annotation { "Feature Type Name" : "Feature", "Feature Type Description" : "" }
export const myFeature = defineFeature(function(context is Context, id is Id, definition is map)
    precondition{}
    {
        {
            var Q0;
            Q0=qCreatedBy(makeId("Front.planeOp"),FACE);
            var sketch = newSketch(context, id + "F0", { "sketchPlane" : qUnion([Q0])});
            skLineSegment(sketch, "E0", {"start": v(0, 0) * mm, "end": v(0, 115.04) * mm, "construction": true});
            skLineSegment(sketch, "E1", {"start": v(0, 54.34) * mm, "end": v(32, 54.34) * mm});
            skLineSegment(sketch, "E2", {"start": v(0, 0) * mm, "end": v(15.73, 0) * mm});
            skFitSpline(sketch, "E3", {"points": [v(32, 54.34) * mm, v(50.29, 47.3) * mm, v(51.95, 34.67) * mm, v(46.18, 14.3) * mm, v(15.73, 0) * mm], "startDerivative": vector(95.6, 0) * mm, "endDerivative": vector(-87.5, 0) * mm});
            skLineSegment(sketch, "E4", {"start": v(0, 54.34) * mm, "end": v(0, 0) * mm});
            skSolve(sketch);
        }
        {
            var Q0;
            Q0=qSketchRegion(id+"F0",true);
            var Q1;
            Q1=sQuery(id+"F0.wireOp",EDGE,"E0");
            revolve(context, id + "F1", {"entities" : qUnion([Q0]), "axis" : qUnion([Q1]), "revolveType" : RevolveType.FULL});
        }
        {
            var Q0;
            Q0=qCreatedBy(makeId("Front.planeOp"),FACE);
            cPlane(context, id + "F2", {"entities" : qUnion([Q0]), "cplaneType" : CPlaneType.OFFSET, "offset" : 55 * mm, "width" : 150 * mm, "height" : 150 * mm});
        }
        {
            var Q0;
            Q0=qCreatedBy(id+"F2.planeOp",FACE);
            var sketch = newSketch(context, id + "F3", { "sketchPlane" : qUnion([Q0])});
            skText(sketch, "E5", { "text": "JAY WILLIAMS", "fontName": "OpenSans-Bold.ttf"});
            const initialGuessF3  = {"E5": [-0.04412, 0.03506, 1, 0, 0.00915]};
            skSetInitialGuess(sketch, initialGuessF3);
            skSolve(sketch);
        }
        {
            var Q0;
            Q0=qSketchRegion(id+"F3",true);
            var Q1;
            Q1=qCreatedBy(makeId("Front.planeOp"),FACE);
            extrude(context, id + "F4", {"entities" : qUnion([Q0]), "endBound" : BoundingType.UP_TO_SURFACE, "oppositeDirection" : true, "endBoundEntityFace" : qUnion([Q1]), "depth" : 25 * mm});
        }
        {
            var Q0;
            Q0=makeQuery(id+"F1.opRevolve","SWEPT_BODY",BODY,{"disambiguationData":[OSD([sQuery(id+"F0.wireOp",EDGE,"E1"),sQuery(id+"F0.wireOp",EDGE,"E2"),sQuery(id+"F0.wireOp",EDGE,"E3"),sQuery(id+"F0.wireOp",EDGE,"E4")])]});
            var Q1;
            Q1=makeQuery(id+"F4.opExtrude","SWEPT_BODY",BODY,{"disambiguationData":[OSD([sQuery(id+"F3.wireOp",EDGE,"E5.sketch_text.stroke-0"),sQuery(id+"F3.wireOp",EDGE,"E5.sketch_text.stroke-1"),sQuery(id+"F3.wireOp",EDGE,"E5.sketch_text.stroke-2"),sQuery(id+"F3.wireOp",EDGE,"E5.sketch_text.stroke-3"),sQuery(id+"F3.wireOp",EDGE,"E5.sketch_text.stroke-4"),sQuery(id+"F3.wireOp",EDGE,"E5.sketch_text.stroke-5"),sQuery(id+"F3.wireOp",EDGE,"E5.sketch_text.stroke-6"),sQuery(id+"F3.wireOp",EDGE,"E5.sketch_text.stroke-7"),sQuery(id+"F3.wireOp",EDGE,"E5.sketch_text.stroke-8"),sQuery(id+"F3.wireOp",EDGE,"E5.sketch_text.stroke-9")])]});
            var Q2;
            Q2=makeQuery(id+"F4.opExtrude","SWEPT_BODY",BODY,{"disambiguationData":[OSD([sQuery(id+"F3.wireOp",EDGE,"E5.sketch_text.stroke-10"),sQuery(id+"F3.wireOp",EDGE,"E5.sketch_text.stroke-11"),sQuery(id+"F3.wireOp",EDGE,"E5.sketch_text.stroke-12"),sQuery(id+"F3.wireOp",EDGE,"E5.sketch_text.stroke-13"),sQuery(id+"F3.wireOp",EDGE,"E5.sketch_text.stroke-14"),sQuery(id+"F3.wireOp",EDGE,"E5.sketch_text.stroke-15"),sQuery(id+"F3.wireOp",EDGE,"E5.sketch_text.stroke-16"),sQuery(id+"F3.wireOp",EDGE,"E5.sketch_text.stroke-17"),sQuery(id+"F3.wireOp",EDGE,"E5.sketch_text.stroke-18"),sQuery(id+"F3.wireOp",EDGE,"E5.sketch_text.stroke-19"),sQuery(id+"F3.wireOp",EDGE,"E5.sketch_text.stroke-20"),sQuery(id+"F3.wireOp",EDGE,"E5.sketch_text.stroke-21")])]});
            var Q3;
            Q3=makeQuery(id+"F4.opExtrude","SWEPT_BODY",BODY,{"disambiguationData":[OSD([sQuery(id+"F3.wireOp",EDGE,"E5.sketch_text.stroke-22"),sQuery(id+"F3.wireOp",EDGE,"E5.sketch_text.stroke-23"),sQuery(id+"F3.wireOp",EDGE,"E5.sketch_text.stroke-24"),sQuery(id+"F3.wireOp",EDGE,"E5.sketch_text.stroke-25"),sQuery(id+"F3.wireOp",EDGE,"E5.sketch_text.stroke-26"),sQuery(id+"F3.wireOp",EDGE,"E5.sketch_text.stroke-27"),sQuery(id+"F3.wireOp",EDGE,"E5.sketch_text.stroke-28"),sQuery(id+"F3.wireOp",EDGE,"E5.sketch_text.stroke-29"),sQuery(id+"F3.wireOp",EDGE,"E5.sketch_text.stroke-30")])]});
            var Q4;
            Q4=makeQuery(id+"F4.opExtrude","SWEPT_BODY",BODY,{"disambiguationData":[OSD([sQuery(id+"F3.wireOp",EDGE,"E5.sketch_text.stroke-31"),sQuery(id+"F3.wireOp",EDGE,"E5.sketch_text.stroke-32"),sQuery(id+"F3.wireOp",EDGE,"E5.sketch_text.stroke-33"),sQuery(id+"F3.wireOp",EDGE,"E5.sketch_text.stroke-34"),sQuery(id+"F3.wireOp",EDGE,"E5.sketch_text.stroke-35"),sQuery(id+"F3.wireOp",EDGE,"E5.sketch_text.stroke-36"),sQuery(id+"F3.wireOp",EDGE,"E5.sketch_text.stroke-37"),sQuery(id+"F3.wireOp",EDGE,"E5.sketch_text.stroke-38"),sQuery(id+"F3.wireOp",EDGE,"E5.sketch_text.stroke-39"),sQuery(id+"F3.wireOp",EDGE,"E5.sketch_text.stroke-40"),sQuery(id+"F3.wireOp",EDGE,"E5.sketch_text.stroke-41"),sQuery(id+"F3.wireOp",EDGE,"E5.sketch_text.stroke-42"),sQuery(id+"F3.wireOp",EDGE,"E5.sketch_text.stroke-43"),sQuery(id+"F3.wireOp",EDGE,"E5.sketch_text.stroke-44"),sQuery(id+"F3.wireOp",EDGE,"E5.sketch_text.stroke-45"),sQuery(id+"F3.wireOp",EDGE,"E5.sketch_text.stroke-46"),sQuery(id+"F3.wireOp",EDGE,"E5.sketch_text.stroke-47"),sQuery(id+"F3.wireOp",EDGE,"E5.sketch_text.stroke-48"),sQuery(id+"F3.wireOp",EDGE,"E5.sketch_text.stroke-49"),sQuery(id+"F3.wireOp",EDGE,"E5.sketch_text.stroke-50"),sQuery(id+"F3.wireOp",EDGE,"E5.sketch_text.stroke-51"),sQuery(id+"F3.wireOp",EDGE,"E5.sketch_text.stroke-52"),sQuery(id+"F3.wireOp",EDGE,"E5.sketch_text.stroke-53"),sQuery(id+"F3.wireOp",EDGE,"E5.sketch_text.stroke-54")])]});
            var Q5;
            Q5=makeQuery(id+"F4.opExtrude","SWEPT_BODY",BODY,{"disambiguationData":[OSD([sQuery(id+"F3.wireOp",EDGE,"E5.sketch_text.stroke-55"),sQuery(id+"F3.wireOp",EDGE,"E5.sketch_text.stroke-56"),sQuery(id+"F3.wireOp",EDGE,"E5.sketch_text.stroke-57"),sQuery(id+"F3.wireOp",EDGE,"E5.sketch_text.stroke-58")])]});
            var Q6;
            Q6=makeQuery(id+"F4.opExtrude","SWEPT_BODY",BODY,{"disambiguationData":[OSD([sQuery(id+"F3.wireOp",EDGE,"E5.sketch_text.stroke-59"),sQuery(id+"F3.wireOp",EDGE,"E5.sketch_text.stroke-60"),sQuery(id+"F3.wireOp",EDGE,"E5.sketch_text.stroke-61"),sQuery(id+"F3.wireOp",EDGE,"E5.sketch_text.stroke-62"),sQuery(id+"F3.wireOp",EDGE,"E5.sketch_text.stroke-63"),sQuery(id+"F3.wireOp",EDGE,"E5.sketch_text.stroke-64")])]});
            var Q7;
            Q7=makeQuery(id+"F4.opExtrude","SWEPT_BODY",BODY,{"disambiguationData":[OSD([sQuery(id+"F3.wireOp",EDGE,"E5.sketch_text.stroke-65"),sQuery(id+"F3.wireOp",EDGE,"E5.sketch_text.stroke-66"),sQuery(id+"F3.wireOp",EDGE,"E5.sketch_text.stroke-67"),sQuery(id+"F3.wireOp",EDGE,"E5.sketch_text.stroke-68"),sQuery(id+"F3.wireOp",EDGE,"E5.sketch_text.stroke-69"),sQuery(id+"F3.wireOp",EDGE,"E5.sketch_text.stroke-70")])]});
            var Q8;
            Q8=makeQuery(id+"F4.opExtrude","SWEPT_BODY",BODY,{"disambiguationData":[OSD([sQuery(id+"F3.wireOp",EDGE,"E5.sketch_text.stroke-71"),sQuery(id+"F3.wireOp",EDGE,"E5.sketch_text.stroke-72"),sQuery(id+"F3.wireOp",EDGE,"E5.sketch_text.stroke-73"),sQuery(id+"F3.wireOp",EDGE,"E5.sketch_text.stroke-74")])]});
            var Q9;
            Q9=makeQuery(id+"F4.opExtrude","SWEPT_BODY",BODY,{"disambiguationData":[OSD([sQuery(id+"F3.wireOp",EDGE,"E5.sketch_text.stroke-75"),sQuery(id+"F3.wireOp",EDGE,"E5.sketch_text.stroke-76"),sQuery(id+"F3.wireOp",EDGE,"E5.sketch_text.stroke-77"),sQuery(id+"F3.wireOp",EDGE,"E5.sketch_text.stroke-78"),sQuery(id+"F3.wireOp",EDGE,"E5.sketch_text.stroke-79"),sQuery(id+"F3.wireOp",EDGE,"E5.sketch_text.stroke-80"),sQuery(id+"F3.wireOp",EDGE,"E5.sketch_text.stroke-81"),sQuery(id+"F3.wireOp",EDGE,"E5.sketch_text.stroke-82"),sQuery(id+"F3.wireOp",EDGE,"E5.sketch_text.stroke-83"),sQuery(id+"F3.wireOp",EDGE,"E5.sketch_text.stroke-84"),sQuery(id+"F3.wireOp",EDGE,"E5.sketch_text.stroke-85"),sQuery(id+"F3.wireOp",EDGE,"E5.sketch_text.stroke-86")])]});
            var Q10;
            Q10=makeQuery(id+"F4.opExtrude","SWEPT_BODY",BODY,{"disambiguationData":[OSD([sQuery(id+"F3.wireOp",EDGE,"E5.sketch_text.stroke-87"),sQuery(id+"F3.wireOp",EDGE,"E5.sketch_text.stroke-88"),sQuery(id+"F3.wireOp",EDGE,"E5.sketch_text.stroke-89"),sQuery(id+"F3.wireOp",EDGE,"E5.sketch_text.stroke-90"),sQuery(id+"F3.wireOp",EDGE,"E5.sketch_text.stroke-91"),sQuery(id+"F3.wireOp",EDGE,"E5.sketch_text.stroke-92"),sQuery(id+"F3.wireOp",EDGE,"E5.sketch_text.stroke-93"),sQuery(id+"F3.wireOp",EDGE,"E5.sketch_text.stroke-94"),sQuery(id+"F3.wireOp",EDGE,"E5.sketch_text.stroke-95"),sQuery(id+"F3.wireOp",EDGE,"E5.sketch_text.stroke-96"),sQuery(id+"F3.wireOp",EDGE,"E5.sketch_text.stroke-97"),sQuery(id+"F3.wireOp",EDGE,"E5.sketch_text.stroke-98"),sQuery(id+"F3.wireOp",EDGE,"E5.sketch_text.stroke-99"),sQuery(id+"F3.wireOp",EDGE,"E5.sketch_text.stroke-100"),sQuery(id+"F3.wireOp",EDGE,"E5.sketch_text.stroke-101"),sQuery(id+"F3.wireOp",EDGE,"E5.sketch_text.stroke-102"),sQuery(id+"F3.wireOp",EDGE,"E5.sketch_text.stroke-103"),sQuery(id+"F3.wireOp",EDGE,"E5.sketch_text.stroke-104"),sQuery(id+"F3.wireOp",EDGE,"E5.sketch_text.stroke-105")])]});
            var Q11;
            Q11=makeQuery(id+"F4.opExtrude","SWEPT_BODY",BODY,{"disambiguationData":[OSD([sQuery(id+"F3.wireOp",EDGE,"E5.sketch_text.stroke-106"),sQuery(id+"F3.wireOp",EDGE,"E5.sketch_text.stroke-107"),sQuery(id+"F3.wireOp",EDGE,"E5.sketch_text.stroke-108"),sQuery(id+"F3.wireOp",EDGE,"E5.sketch_text.stroke-109"),sQuery(id+"F3.wireOp",EDGE,"E5.sketch_text.stroke-110"),sQuery(id+"F3.wireOp",EDGE,"E5.sketch_text.stroke-111"),sQuery(id+"F3.wireOp",EDGE,"E5.sketch_text.stroke-112"),sQuery(id+"F3.wireOp",EDGE,"E5.sketch_text.stroke-113"),sQuery(id+"F3.wireOp",EDGE,"E5.sketch_text.stroke-114"),sQuery(id+"F3.wireOp",EDGE,"E5.sketch_text.stroke-115"),sQuery(id+"F3.wireOp",EDGE,"E5.sketch_text.stroke-116"),sQuery(id+"F3.wireOp",EDGE,"E5.sketch_text.stroke-117"),sQuery(id+"F3.wireOp",EDGE,"E5.sketch_text.stroke-118"),sQuery(id+"F3.wireOp",EDGE,"E5.sketch_text.stroke-119"),sQuery(id+"F3.wireOp",EDGE,"E5.sketch_text.stroke-120"),sQuery(id+"F3.wireOp",EDGE,"E5.sketch_text.stroke-121"),sQuery(id+"F3.wireOp",EDGE,"E5.sketch_text.stroke-122"),sQuery(id+"F3.wireOp",EDGE,"E5.sketch_text.stroke-123"),sQuery(id+"F3.wireOp",EDGE,"E5.sketch_text.stroke-124"),sQuery(id+"F3.wireOp",EDGE,"E5.sketch_text.stroke-125"),sQuery(id+"F3.wireOp",EDGE,"E5.sketch_text.stroke-126"),sQuery(id+"F3.wireOp",EDGE,"E5.sketch_text.stroke-127"),sQuery(id+"F3.wireOp",EDGE,"E5.sketch_text.stroke-128"),sQuery(id+"F3.wireOp",EDGE,"E5.sketch_text.stroke-129"),sQuery(id+"F3.wireOp",EDGE,"E5.sketch_text.stroke-130"),sQuery(id+"F3.wireOp",EDGE,"E5.sketch_text.stroke-131"),sQuery(id+"F3.wireOp",EDGE,"E5.sketch_text.stroke-132"),sQuery(id+"F3.wireOp",EDGE,"E5.sketch_text.stroke-133")])]});
            booleanBodies(context, id + "F5", {"operationType" : BooleanOperationType.SUBTRACTION, "tools" : qUnion([Q0]), "targets" : qUnion([Q1, Q2, Q3, Q4, Q5, Q6, Q7, Q8, Q9, Q10, Q11]), "offset" : true, "offsetAll" : true, "offsetDistance" : 1.5 * mm, "oppositeDirection" : true, "keepTools" : true});
        }
        {
            var Q0;
            Q0=makeQuery(id+"F4.opExtrude","SWEPT_BODY",BODY,{"disambiguationData":[OSD([sQuery(id+"F3.wireOp",EDGE,"E5.sketch_text.stroke-0"),sQuery(id+"F3.wireOp",EDGE,"E5.sketch_text.stroke-1"),sQuery(id+"F3.wireOp",EDGE,"E5.sketch_text.stroke-2"),sQuery(id+"F3.wireOp",EDGE,"E5.sketch_text.stroke-3"),sQuery(id+"F3.wireOp",EDGE,"E5.sketch_text.stroke-4"),sQuery(id+"F3.wireOp",EDGE,"E5.sketch_text.stroke-5"),sQuery(id+"F3.wireOp",EDGE,"E5.sketch_text.stroke-6"),sQuery(id+"F3.wireOp",EDGE,"E5.sketch_text.stroke-7"),sQuery(id+"F3.wireOp",EDGE,"E5.sketch_text.stroke-8"),sQuery(id+"F3.wireOp",EDGE,"E5.sketch_text.stroke-9")])]});
            var Q1;
            Q1=makeQuery(id+"F4.opExtrude","SWEPT_BODY",BODY,{"disambiguationData":[OSD([sQuery(id+"F3.wireOp",EDGE,"E5.sketch_text.stroke-10"),sQuery(id+"F3.wireOp",EDGE,"E5.sketch_text.stroke-11"),sQuery(id+"F3.wireOp",EDGE,"E5.sketch_text.stroke-12"),sQuery(id+"F3.wireOp",EDGE,"E5.sketch_text.stroke-13"),sQuery(id+"F3.wireOp",EDGE,"E5.sketch_text.stroke-14"),sQuery(id+"F3.wireOp",EDGE,"E5.sketch_text.stroke-15"),sQuery(id+"F3.wireOp",EDGE,"E5.sketch_text.stroke-16"),sQuery(id+"F3.wireOp",EDGE,"E5.sketch_text.stroke-17"),sQuery(id+"F3.wireOp",EDGE,"E5.sketch_text.stroke-18"),sQuery(id+"F3.wireOp",EDGE,"E5.sketch_text.stroke-19"),sQuery(id+"F3.wireOp",EDGE,"E5.sketch_text.stroke-20"),sQuery(id+"F3.wireOp",EDGE,"E5.sketch_text.stroke-21")])]});
            var Q2;
            Q2=makeQuery(id+"F4.opExtrude","SWEPT_BODY",BODY,{"disambiguationData":[OSD([sQuery(id+"F3.wireOp",EDGE,"E5.sketch_text.stroke-22"),sQuery(id+"F3.wireOp",EDGE,"E5.sketch_text.stroke-23"),sQuery(id+"F3.wireOp",EDGE,"E5.sketch_text.stroke-24"),sQuery(id+"F3.wireOp",EDGE,"E5.sketch_text.stroke-25"),sQuery(id+"F3.wireOp",EDGE,"E5.sketch_text.stroke-26"),sQuery(id+"F3.wireOp",EDGE,"E5.sketch_text.stroke-27"),sQuery(id+"F3.wireOp",EDGE,"E5.sketch_text.stroke-28"),sQuery(id+"F3.wireOp",EDGE,"E5.sketch_text.stroke-29"),sQuery(id+"F3.wireOp",EDGE,"E5.sketch_text.stroke-30")])]});
            var Q3;
            Q3=makeQuery(id+"F4.opExtrude","SWEPT_BODY",BODY,{"disambiguationData":[OSD([sQuery(id+"F3.wireOp",EDGE,"E5.sketch_text.stroke-31"),sQuery(id+"F3.wireOp",EDGE,"E5.sketch_text.stroke-32"),sQuery(id+"F3.wireOp",EDGE,"E5.sketch_text.stroke-33"),sQuery(id+"F3.wireOp",EDGE,"E5.sketch_text.stroke-34"),sQuery(id+"F3.wireOp",EDGE,"E5.sketch_text.stroke-35"),sQuery(id+"F3.wireOp",EDGE,"E5.sketch_text.stroke-36"),sQuery(id+"F3.wireOp",EDGE,"E5.sketch_text.stroke-37"),sQuery(id+"F3.wireOp",EDGE,"E5.sketch_text.stroke-38"),sQuery(id+"F3.wireOp",EDGE,"E5.sketch_text.stroke-39"),sQuery(id+"F3.wireOp",EDGE,"E5.sketch_text.stroke-40"),sQuery(id+"F3.wireOp",EDGE,"E5.sketch_text.stroke-41"),sQuery(id+"F3.wireOp",EDGE,"E5.sketch_text.stroke-42"),sQuery(id+"F3.wireOp",EDGE,"E5.sketch_text.stroke-43"),sQuery(id+"F3.wireOp",EDGE,"E5.sketch_text.stroke-44"),sQuery(id+"F3.wireOp",EDGE,"E5.sketch_text.stroke-45"),sQuery(id+"F3.wireOp",EDGE,"E5.sketch_text.stroke-46"),sQuery(id+"F3.wireOp",EDGE,"E5.sketch_text.stroke-47"),sQuery(id+"F3.wireOp",EDGE,"E5.sketch_text.stroke-48"),sQuery(id+"F3.wireOp",EDGE,"E5.sketch_text.stroke-49"),sQuery(id+"F3.wireOp",EDGE,"E5.sketch_text.stroke-50"),sQuery(id+"F3.wireOp",EDGE,"E5.sketch_text.stroke-51"),sQuery(id+"F3.wireOp",EDGE,"E5.sketch_text.stroke-52"),sQuery(id+"F3.wireOp",EDGE,"E5.sketch_text.stroke-53"),sQuery(id+"F3.wireOp",EDGE,"E5.sketch_text.stroke-54")])]});
            var Q4;
            Q4=makeQuery(id+"F4.opExtrude","SWEPT_BODY",BODY,{"disambiguationData":[OSD([sQuery(id+"F3.wireOp",EDGE,"E5.sketch_text.stroke-55"),sQuery(id+"F3.wireOp",EDGE,"E5.sketch_text.stroke-56"),sQuery(id+"F3.wireOp",EDGE,"E5.sketch_text.stroke-57"),sQuery(id+"F3.wireOp",EDGE,"E5.sketch_text.stroke-58")])]});
            var Q5;
            Q5=makeQuery(id+"F4.opExtrude","SWEPT_BODY",BODY,{"disambiguationData":[OSD([sQuery(id+"F3.wireOp",EDGE,"E5.sketch_text.stroke-59"),sQuery(id+"F3.wireOp",EDGE,"E5.sketch_text.stroke-60"),sQuery(id+"F3.wireOp",EDGE,"E5.sketch_text.stroke-61"),sQuery(id+"F3.wireOp",EDGE,"E5.sketch_text.stroke-62"),sQuery(id+"F3.wireOp",EDGE,"E5.sketch_text.stroke-63"),sQuery(id+"F3.wireOp",EDGE,"E5.sketch_text.stroke-64")])]});
            var Q6;
            Q6=makeQuery(id+"F4.opExtrude","SWEPT_BODY",BODY,{"disambiguationData":[OSD([sQuery(id+"F3.wireOp",EDGE,"E5.sketch_text.stroke-65"),sQuery(id+"F3.wireOp",EDGE,"E5.sketch_text.stroke-66"),sQuery(id+"F3.wireOp",EDGE,"E5.sketch_text.stroke-67"),sQuery(id+"F3.wireOp",EDGE,"E5.sketch_text.stroke-68"),sQuery(id+"F3.wireOp",EDGE,"E5.sketch_text.stroke-69"),sQuery(id+"F3.wireOp",EDGE,"E5.sketch_text.stroke-70")])]});
            var Q7;
            Q7=makeQuery(id+"F4.opExtrude","SWEPT_BODY",BODY,{"disambiguationData":[OSD([sQuery(id+"F3.wireOp",EDGE,"E5.sketch_text.stroke-71"),sQuery(id+"F3.wireOp",EDGE,"E5.sketch_text.stroke-72"),sQuery(id+"F3.wireOp",EDGE,"E5.sketch_text.stroke-73"),sQuery(id+"F3.wireOp",EDGE,"E5.sketch_text.stroke-74")])]});
            var Q8;
            Q8=makeQuery(id+"F4.opExtrude","SWEPT_BODY",BODY,{"disambiguationData":[OSD([sQuery(id+"F3.wireOp",EDGE,"E5.sketch_text.stroke-75"),sQuery(id+"F3.wireOp",EDGE,"E5.sketch_text.stroke-76"),sQuery(id+"F3.wireOp",EDGE,"E5.sketch_text.stroke-77"),sQuery(id+"F3.wireOp",EDGE,"E5.sketch_text.stroke-78"),sQuery(id+"F3.wireOp",EDGE,"E5.sketch_text.stroke-79"),sQuery(id+"F3.wireOp",EDGE,"E5.sketch_text.stroke-80"),sQuery(id+"F3.wireOp",EDGE,"E5.sketch_text.stroke-81"),sQuery(id+"F3.wireOp",EDGE,"E5.sketch_text.stroke-82"),sQuery(id+"F3.wireOp",EDGE,"E5.sketch_text.stroke-83"),sQuery(id+"F3.wireOp",EDGE,"E5.sketch_text.stroke-84"),sQuery(id+"F3.wireOp",EDGE,"E5.sketch_text.stroke-85"),sQuery(id+"F3.wireOp",EDGE,"E5.sketch_text.stroke-86")])]});
            var Q9;
            Q9=makeQuery(id+"F4.opExtrude","SWEPT_BODY",BODY,{"disambiguationData":[OSD([sQuery(id+"F3.wireOp",EDGE,"E5.sketch_text.stroke-87"),sQuery(id+"F3.wireOp",EDGE,"E5.sketch_text.stroke-88"),sQuery(id+"F3.wireOp",EDGE,"E5.sketch_text.stroke-89"),sQuery(id+"F3.wireOp",EDGE,"E5.sketch_text.stroke-90"),sQuery(id+"F3.wireOp",EDGE,"E5.sketch_text.stroke-91"),sQuery(id+"F3.wireOp",EDGE,"E5.sketch_text.stroke-92"),sQuery(id+"F3.wireOp",EDGE,"E5.sketch_text.stroke-93"),sQuery(id+"F3.wireOp",EDGE,"E5.sketch_text.stroke-94"),sQuery(id+"F3.wireOp",EDGE,"E5.sketch_text.stroke-95"),sQuery(id+"F3.wireOp",EDGE,"E5.sketch_text.stroke-96"),sQuery(id+"F3.wireOp",EDGE,"E5.sketch_text.stroke-97"),sQuery(id+"F3.wireOp",EDGE,"E5.sketch_text.stroke-98"),sQuery(id+"F3.wireOp",EDGE,"E5.sketch_text.stroke-99"),sQuery(id+"F3.wireOp",EDGE,"E5.sketch_text.stroke-100"),sQuery(id+"F3.wireOp",EDGE,"E5.sketch_text.stroke-101"),sQuery(id+"F3.wireOp",EDGE,"E5.sketch_text.stroke-102"),sQuery(id+"F3.wireOp",EDGE,"E5.sketch_text.stroke-103"),sQuery(id+"F3.wireOp",EDGE,"E5.sketch_text.stroke-104"),sQuery(id+"F3.wireOp",EDGE,"E5.sketch_text.stroke-105")])]});
            var Q10;
            Q10=makeQuery(id+"F4.opExtrude","SWEPT_BODY",BODY,{"disambiguationData":[OSD([sQuery(id+"F3.wireOp",EDGE,"E5.sketch_text.stroke-106"),sQuery(id+"F3.wireOp",EDGE,"E5.sketch_text.stroke-107"),sQuery(id+"F3.wireOp",EDGE,"E5.sketch_text.stroke-108"),sQuery(id+"F3.wireOp",EDGE,"E5.sketch_text.stroke-109"),sQuery(id+"F3.wireOp",EDGE,"E5.sketch_text.stroke-110"),sQuery(id+"F3.wireOp",EDGE,"E5.sketch_text.stroke-111"),sQuery(id+"F3.wireOp",EDGE,"E5.sketch_text.stroke-112"),sQuery(id+"F3.wireOp",EDGE,"E5.sketch_text.stroke-113"),sQuery(id+"F3.wireOp",EDGE,"E5.sketch_text.stroke-114"),sQuery(id+"F3.wireOp",EDGE,"E5.sketch_text.stroke-115"),sQuery(id+"F3.wireOp",EDGE,"E5.sketch_text.stroke-116"),sQuery(id+"F3.wireOp",EDGE,"E5.sketch_text.stroke-117"),sQuery(id+"F3.wireOp",EDGE,"E5.sketch_text.stroke-118"),sQuery(id+"F3.wireOp",EDGE,"E5.sketch_text.stroke-119"),sQuery(id+"F3.wireOp",EDGE,"E5.sketch_text.stroke-120"),sQuery(id+"F3.wireOp",EDGE,"E5.sketch_text.stroke-121"),sQuery(id+"F3.wireOp",EDGE,"E5.sketch_text.stroke-122"),sQuery(id+"F3.wireOp",EDGE,"E5.sketch_text.stroke-123"),sQuery(id+"F3.wireOp",EDGE,"E5.sketch_text.stroke-124"),sQuery(id+"F3.wireOp",EDGE,"E5.sketch_text.stroke-125"),sQuery(id+"F3.wireOp",EDGE,"E5.sketch_text.stroke-126"),sQuery(id+"F3.wireOp",EDGE,"E5.sketch_text.stroke-127"),sQuery(id+"F3.wireOp",EDGE,"E5.sketch_text.stroke-128"),sQuery(id+"F3.wireOp",EDGE,"E5.sketch_text.stroke-129"),sQuery(id+"F3.wireOp",EDGE,"E5.sketch_text.stroke-130"),sQuery(id+"F3.wireOp",EDGE,"E5.sketch_text.stroke-131"),sQuery(id+"F3.wireOp",EDGE,"E5.sketch_text.stroke-132"),sQuery(id+"F3.wireOp",EDGE,"E5.sketch_text.stroke-133")])]});
            var Q11;
            Q11=makeQuery(id+"F1.opRevolve","SWEPT_BODY",BODY,{"disambiguationData":[OSD([sQuery(id+"F0.wireOp",EDGE,"E1"),sQuery(id+"F0.wireOp",EDGE,"E2"),sQuery(id+"F0.wireOp",EDGE,"E3"),sQuery(id+"F0.wireOp",EDGE,"E4")])]});
            booleanBodies(context, id + "F6", {"operationType" : BooleanOperationType.SUBTRACTION, "tools" : qUnion([Q0, Q1, Q2, Q3, Q4, Q5, Q6, Q7, Q8, Q9, Q10]), "targets" : qUnion([Q11])});
        }
    });